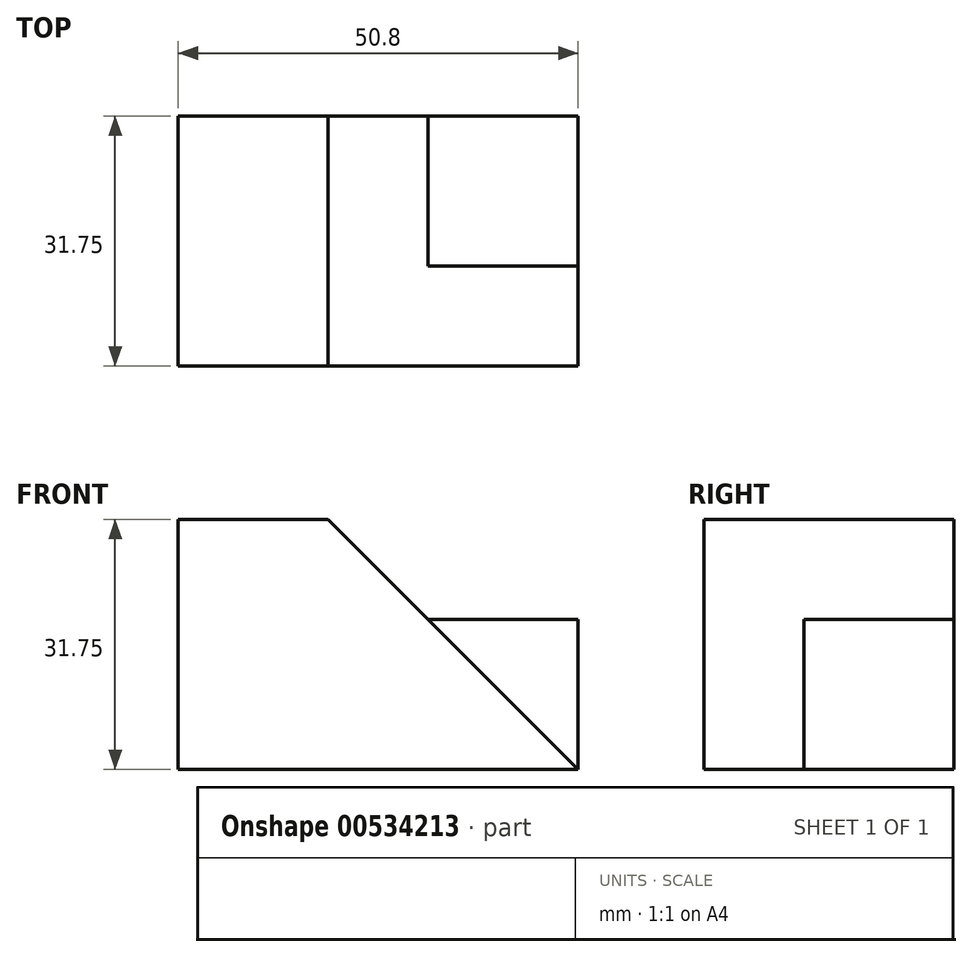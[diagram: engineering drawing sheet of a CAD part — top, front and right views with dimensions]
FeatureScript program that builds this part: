
annotation { "Feature Type Name" : "Feature", "Feature Type Description" : "" }
export const myFeature = defineFeature(function(context is Context, id is Id, definition is map)
    precondition{}
    {
        {
            var Q0;
            Q0=qCreatedBy(makeId("Front.planeOp"),FACE);
            var sketch = newSketch(context, id + "F0", { "sketchPlane" : qUnion([Q0])});
            skLineSegment(sketch, "E0", {"start": v(0, 0) * mm, "end": v(50.8, 0) * mm});
            skLineSegment(sketch, "E1", {"start": v(50.8, 0) * mm, "end": v(50.8, 31.75) * mm});
            skLineSegment(sketch, "E2", {"start": v(50.8, 31.75) * mm, "end": v(0, 31.75) * mm});
            skLineSegment(sketch, "E3", {"start": v(0, 31.75) * mm, "end": v(0, 0) * mm});
            skSolve(sketch);
        }
        {
            var Q0;
            Q0=makeQuery(id+"F0.imprint","IMPRINT",FACE,{"disambiguationData":[TD([[makeQuery(id+"F0.imprint","IMPRINT",EDGE,{"derivedFrom":sQuery(id+"F0.wireOp",EDGE,"E0")}),1.0]])]});
            extrude(context, id + "F1", {"entities" : qUnion([Q0]), "depth" : 31.75 * mm, "offsetDistance" : 25.4 * mm});
        }
        {
            var Q0;
            Q0=makeQuery(id+"F1.opExtrude","CAP_FACE",FACE,{"disambiguationData":[OSD([sQuery(id+"F0.wireOp",EDGE,"E0"),sQuery(id+"F0.wireOp",EDGE,"E1"),sQuery(id+"F0.wireOp",EDGE,"E2"),sQuery(id+"F0.wireOp",EDGE,"E3")])],"isStart":false});
            var sketch = newSketch(context, id + "F2", { "sketchPlane" : qUnion([Q0])});
            skLineSegment(sketch, "E4", {"start": v(50.8, 0) * mm, "end": v(19.05, 31.75) * mm});
            skLineSegment(sketch, "E5", {"start": v(19.05, 31.75) * mm, "end": v(50.8, 31.75) * mm});
            skLineSegment(sketch, "E6", {"start": v(50.8, 31.75) * mm, "end": v(50.8, 0) * mm});
            skSolve(sketch);
        }
        {
            var Q0;
            Q0=makeQuery(id+"F2.imprint","IMPRINT",FACE,{"disambiguationData":[TD([[makeQuery(id+"F2.imprint","IMPRINT",EDGE,{"derivedFrom":sQuery(id+"F2.wireOp",EDGE,"E4")}),-1.0]])]});
            extrude(context, id + "F3", {"entities" : qUnion([Q0]), "operationType" : NewBodyOperationType.REMOVE, "oppositeDirection" : true, "depth" : 12.7 * mm, "offsetDistance" : 25.4 * mm});
        }
        {
            var Q0;
            Q0=makeQuery(id+"F3.boolean.opBoolean","COPY",FACE,{"derivedFrom":makeQuery(id+"F3.opExtrude","CAP_FACE",FACE,{"disambiguationData":[OSD([sQuery(id+"F2.wireOp",EDGE,"E4"),sQuery(id+"F2.wireOp",EDGE,"E5"),sQuery(id+"F2.wireOp",EDGE,"E6")])],"isStart":false})});
            var sketch = newSketch(context, id + "F4", { "sketchPlane" : qUnion([Q0])});
            skLineSegment(sketch, "E7", {"start": v(50.8, 19.05) * mm, "end": v(31.75, 19.05) * mm});
            skLineSegment(sketch, "E8", {"start": v(50.8, 19.05) * mm, "end": v(50.8, 31.75) * mm});
            skLineSegment(sketch, "E9", {"start": v(50.8, 31.75) * mm, "end": v(19.05, 31.75) * mm});
            skLineSegment(sketch, "E10", {"start": v(19.05, 31.75) * mm, "end": v(31.75, 19.05) * mm});
            skSolve(sketch);
        }
        {
            var Q0;
            Q0=makeQuery(id+"F4.imprint","IMPRINT",FACE,{"disambiguationData":[TD([[makeQuery(id+"F4.imprint","IMPRINT",EDGE,{"derivedFrom":sQuery(id+"F4.wireOp",EDGE,"E7")}),-1.0]])]});
            extrude(context, id + "F5", {"entities" : qUnion([Q0]), "operationType" : NewBodyOperationType.REMOVE, "oppositeDirection" : true, "depth" : 19.05 * mm, "offsetDistance" : 25.4 * mm});
        }
    });
